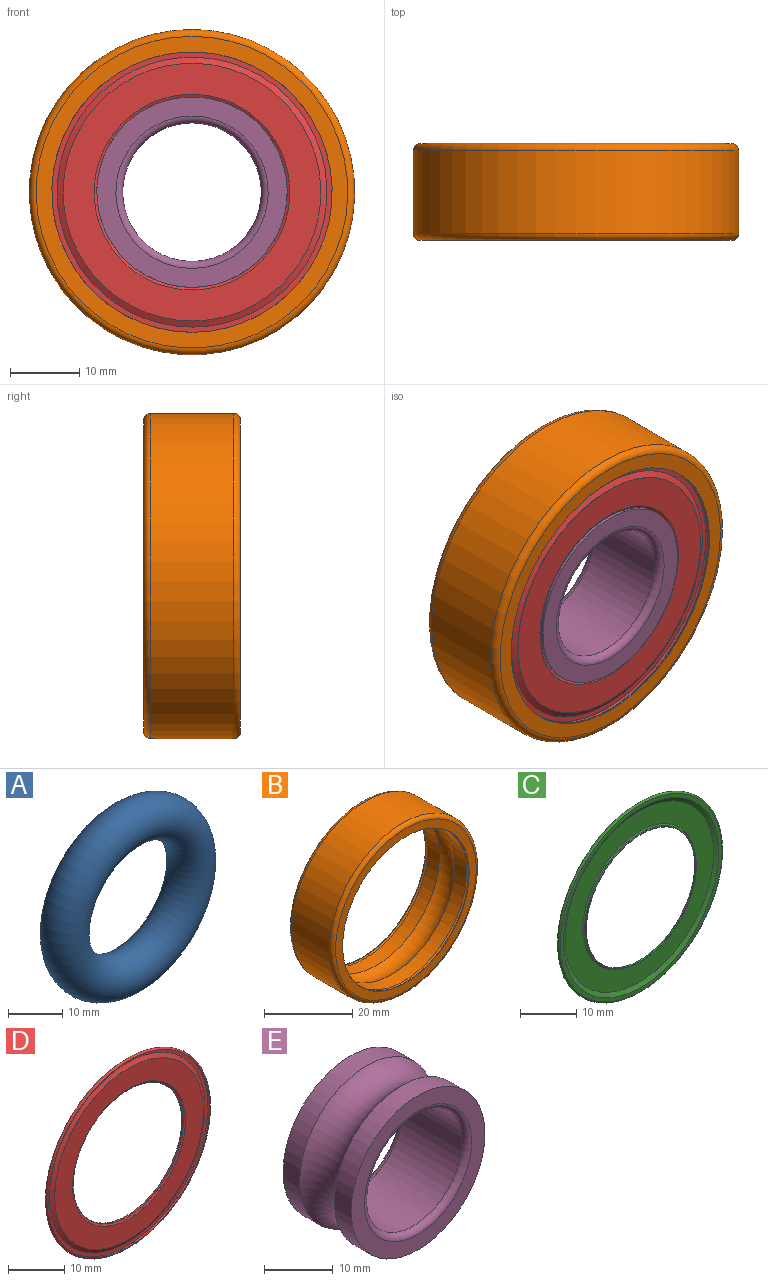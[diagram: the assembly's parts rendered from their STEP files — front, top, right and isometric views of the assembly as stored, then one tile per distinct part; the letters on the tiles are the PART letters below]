
ASSEMBLY  parts=5 mates=8
PART A: 1 faces, bbox 45.5x9x45.5 mm
  f0: torus R=16.5mm, axis (0,-1,0), area 2931.3mm2
PART B: 12 faces, bbox 50.9x14x50.9 mm
  f0: torus R=16.5mm, axis (0,-1,0), area 687.1mm2, adj f1,f9
  f1: cylinder r=20.25mm len=40.5mm, axis (0,-1,0), area 476.2mm2, adj f0,f2
  f2: torus R=20.25mm, axis (0,-1,0), area 121mm2, adj f1,f3
  f3: cylinder r=20.25mm len=40.5mm, axis (0,-1,0), area 21.6mm2, adj f2,f4
  f4: plane 45x45mm, normal (0,1,0), area 302.2mm2, adj f3,f10
  f5: cylinder r=23.5mm len=47mm, axis (0,-1,0), area 1771.9mm2, adj f10,f11
  f6: plane 45x45mm, normal (0,-1,0), area 302.2mm2, adj f7,f11
  f7: cylinder r=20.25mm len=40.5mm, axis (0,-1,0), area 21.6mm2, adj f6,f8
  f8: torus R=20.25mm, axis (0,-1,0), area 121mm2, adj f7,f9
  f9: cylinder r=20.25mm len=40.5mm, axis (0,-1,0), area 476.2mm2, adj f0,f8
  f10: torus R=22.5mm, axis (0,1,0), area 228.3mm2, adj f4,f5
  f11: torus R=22.5mm, axis (0,1,0), area 228.3mm2, adj f5,f6
PART C: 14 faces, bbox 44.5x0.6x44.5 mm
  f0: plane 27.7x27.7mm, normal (0,-1,0), area 8.7mm2, adj f7,f13
  f1: cylinder r=20.25mm len=40.5mm, axis (0,-1,0), area 12.7mm2, adj f2,f8
  f2: torus R=20.25mm, axis (0,-1,0), area 121mm2, adj f1,f3
  f3: plane 40.5x40.5mm, normal (0,-1,0), area 97.3mm2, adj f2,f4
  f4: cone r=18.59mm half-angle=61.9deg, axis (0,-1,0), area 119.3mm2, adj f3,f5
  f5: plane 37.18x37.18mm, normal (0,-1,0), area 454.9mm2, adj f4,f6
  f6: cone r=13.85mm half-angle=62deg, axis (0,1,0), area 31.9mm2, adj f5,f7
  f7: cylinder r=13.85mm len=27.7mm, axis (0,-1,0), area 26.1mm2, adj f0,f6
  f8: torus R=20.25mm, axis (0,-1,0), area 80.4mm2, adj f1,f9
  f9: plane 40.5x40.5mm, normal (0,1,0), area 94.3mm2, adj f8,f10
  f10: cone r=18.64mm half-angle=61.9deg, axis (0,-1,0), area 119.4mm2, adj f9,f11
  f11: plane 37.23x37.23mm, normal (0,1,0), area 460mm2, adj f10,f12
  f12: cone r=13.8mm half-angle=62deg, axis (0,1,0), area 39.2mm2, adj f11,f13
  f13: cylinder r=13.75mm len=27.5mm, axis (0,-1,0), area 31.1mm2, adj f0,f12
PART D: 14 faces, bbox 44.5x0.6x44.5 mm
  f0: plane 27.7x27.7mm, normal (0,1,0), area 8.7mm2, adj f7,f13
  f1: cylinder r=20.25mm len=40.5mm, axis (0,1,0), area 12.7mm2, adj f2,f8
  f2: torus R=20.25mm, axis (0,1,0), area 121mm2, adj f1,f3
  f3: plane 40.5x40.5mm, normal (0,1,0), area 97.3mm2, adj f2,f4
  f4: cone r=18.59mm half-angle=61.9deg, axis (0,1,0), area 119.3mm2, adj f3,f5
  f5: plane 37.18x37.18mm, normal (0,1,0), area 454.9mm2, adj f4,f6
  f6: cone r=13.85mm half-angle=62deg, axis (0,-1,0), area 31.9mm2, adj f5,f7
  f7: cylinder r=13.85mm len=27.7mm, axis (0,1,0), area 26.1mm2, adj f0,f6
  f8: torus R=20.25mm, axis (0,1,0), area 80.4mm2, adj f1,f9
  f9: plane 40.5x40.5mm, normal (0,-1,0), area 94.3mm2, adj f8,f10
  f10: cone r=18.64mm half-angle=61.9deg, axis (0,1,0), area 119.4mm2, adj f9,f11
  f11: plane 37.23x37.23mm, normal (0,-1,0), area 460mm2, adj f10,f12
  f12: cone r=13.8mm half-angle=62deg, axis (0,-1,0), area 39.2mm2, adj f11,f13
  f13: cylinder r=13.75mm len=27.5mm, axis (0,1,0), area 31.1mm2, adj f0,f12
PART E: 8 faces, bbox 35.7x14x35.7 mm
  f0: plane 27.5x27.5mm, normal (0,-1,0), area 213.8mm2, adj f5,f6
  f1: cylinder r=10mm len=20mm, axis (0,-1,0), area 754mm2, adj f6,f7
  f2: plane 27.5x27.5mm, normal (0,1,0), area 213.8mm2, adj f3,f7
  f3: cylinder r=13.75mm len=27.5mm, axis (0,-1,0), area 297mm2, adj f2,f4
  f4: torus R=16.5mm, axis (0,-1,0), area 650.8mm2, adj f3,f5
  f5: cylinder r=13.75mm len=27.5mm, axis (0,-1,0), area 297mm2, adj f0,f4
  f6: torus R=11mm, axis (0,1,0), area 102.3mm2, adj f0,f1
  f7: torus R=11mm, axis (0,1,0), area 102.3mm2, adj f1,f2
PLACE A at identity
PLACE B at identity
PLACE C rot(axis=(0,1,0),2.8deg) t=(0,0,0)mm
PLACE D rot(axis=(0,1,0),2.8deg) t=(0,0,0)mm
PLACE E at identity fixed
MATE ball B.f0 <-> C.f1  axis (0,-1,0) through (0,6.53,0)mm
MATE planar B.f0 <-> E.f1  axis (0,-1,0) through (0,0,0)mm
MATE ball B.f0 <-> A.f0  axis (0,-1,0) through (0,0,0)mm
MATE ball D.f1 <-> B.f0  axis (0,1,0) through (0,-6.53,0)mm
MATE parallel C.f1 <-> E.f1  axis (0,1,0) through (0,6.8,0)mm
MATE ball A.f0 <-> E.f1  axis (0,-1,0) through (0,0,0)mm
MATE planar A.f0 <-> E.f1  axis (0,-1,0) through (0,0,0)mm
MATE parallel D.f1 <-> E.f1  axis (0,-1,0) through (0,-6.8,0)mm
